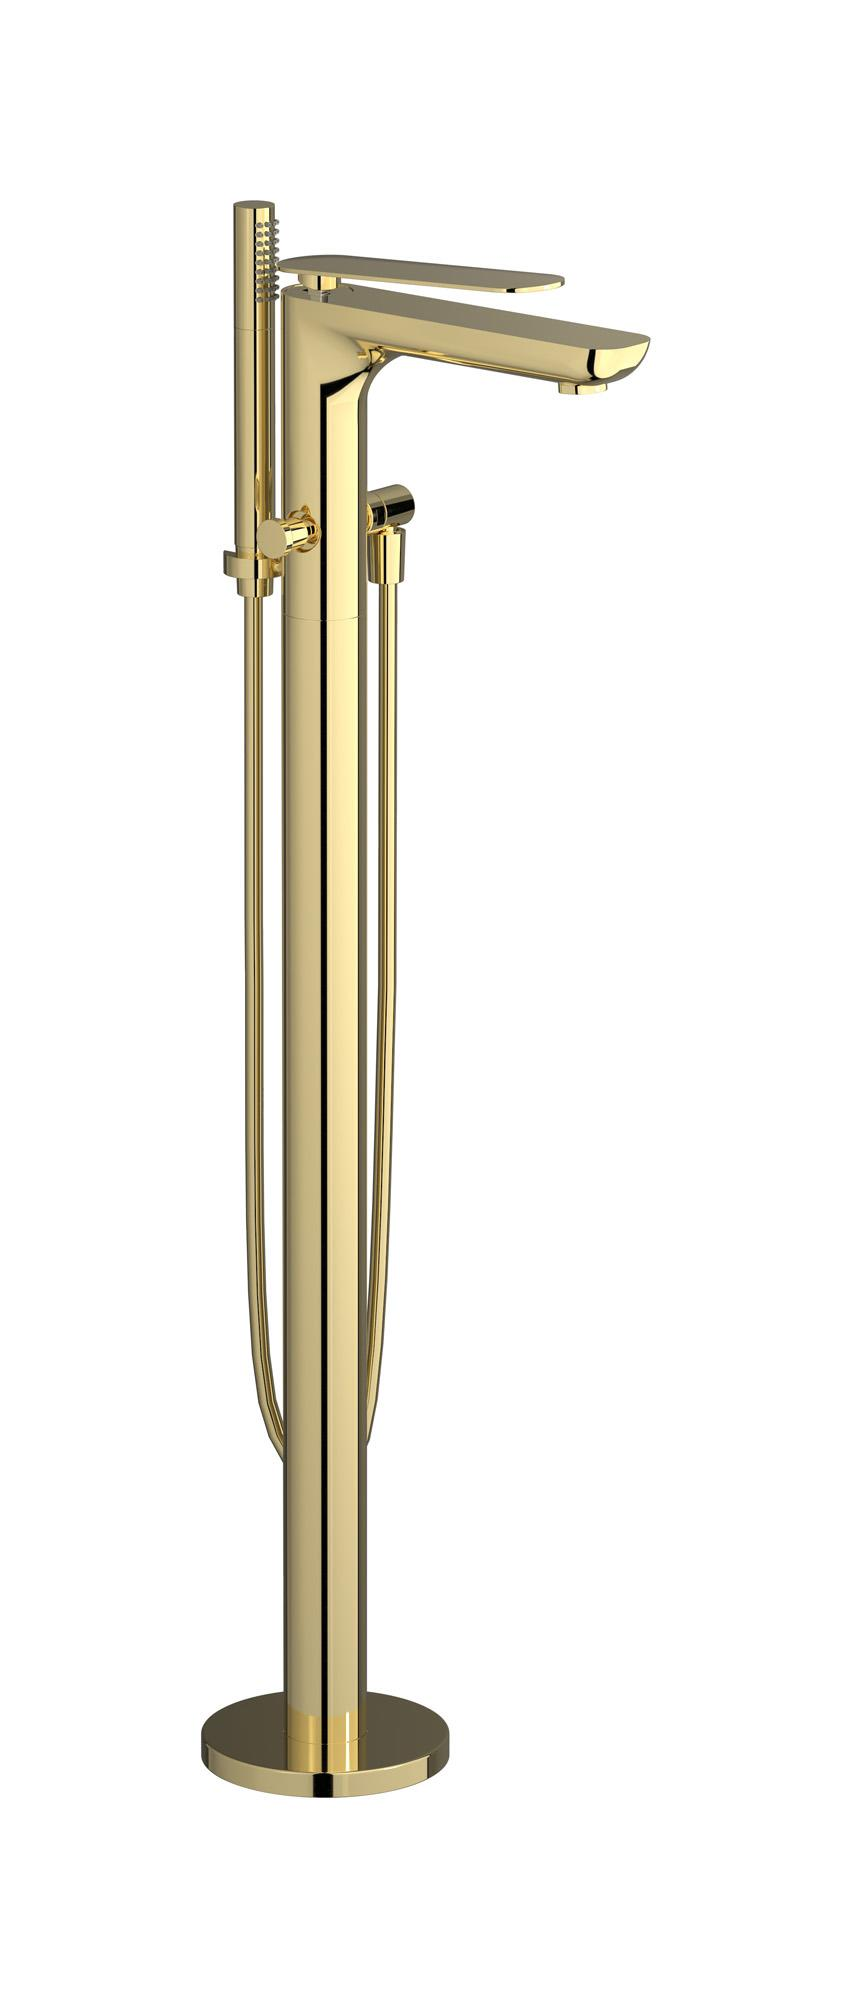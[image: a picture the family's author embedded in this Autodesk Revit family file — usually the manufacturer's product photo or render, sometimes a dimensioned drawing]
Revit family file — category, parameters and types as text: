
# Revit family: K2399
name_source: partatom
category: Apparecchi idraulici
units: mm (PartAtom-declared; Revit-internal decimal feet)

## family parameters
Basato su piano di lavoro = No
Condiviso = No
Mantieni orientamento annotazione = No
Numero OmniClass = 23.45.55.17
Punto di calcolo locali = No
Quota connettore circolare = Usa diametro
Sempre verticale = Sì
Taglio con vuoti quando caricato = No
Tipo di parte = Normale
Titolo OmniClass = Mixing Faucets

## types (9) — shared parameters
Cold water inlet = 10 mm  [stored 0.0328084 ft]
Commenti sul tipo = Freestanding bath filler
Connessione CW = No
Connessione HW = No
Connessione di scarico = No
Connessione di ventilazione = No
Descrizione = Freestanding bath filler
Hot water inlet = 10 mm  [stored 0.0328084 ft]
Produttore = IB Rubinetterie S.p.A.
URL = https://www.weareib.it
zero-valued in all types: Prospetto di default

## per-type parameters (varying)
| type | Finishes surface | Immagine tipo | Modello |
| Chrome | IB_Chrome | K2399CC.jpg | K2399CC |
| Brushed nickel | IB_Brushed nickel | K2399SS.jpg | K2399SS |
| Matt black | IB_matt black | K2399NP.jpg | K2399NP |
| Matt white | IB_matt white | K2399BO.jpg | K2399BO |
| Platinum | IB_Platinum | K2399PL.jpg | K2399PL |
| Pale gold | IB_Pale gold | K2399II.jpg | K2399II |
| Brushed pale gold | IB_brushed pale gold | K2399IS.jpg | K2399IS |
| Rose gold | IB_Rose gold | K2399RS.jpg | K2399RS |
| Gold | IB_gold | K2399OO.jpg | K2399OO |

note: [stored X ft] marks values corroborated as IEEE doubles in the binary element streams (Revit-internal decimal feet)
